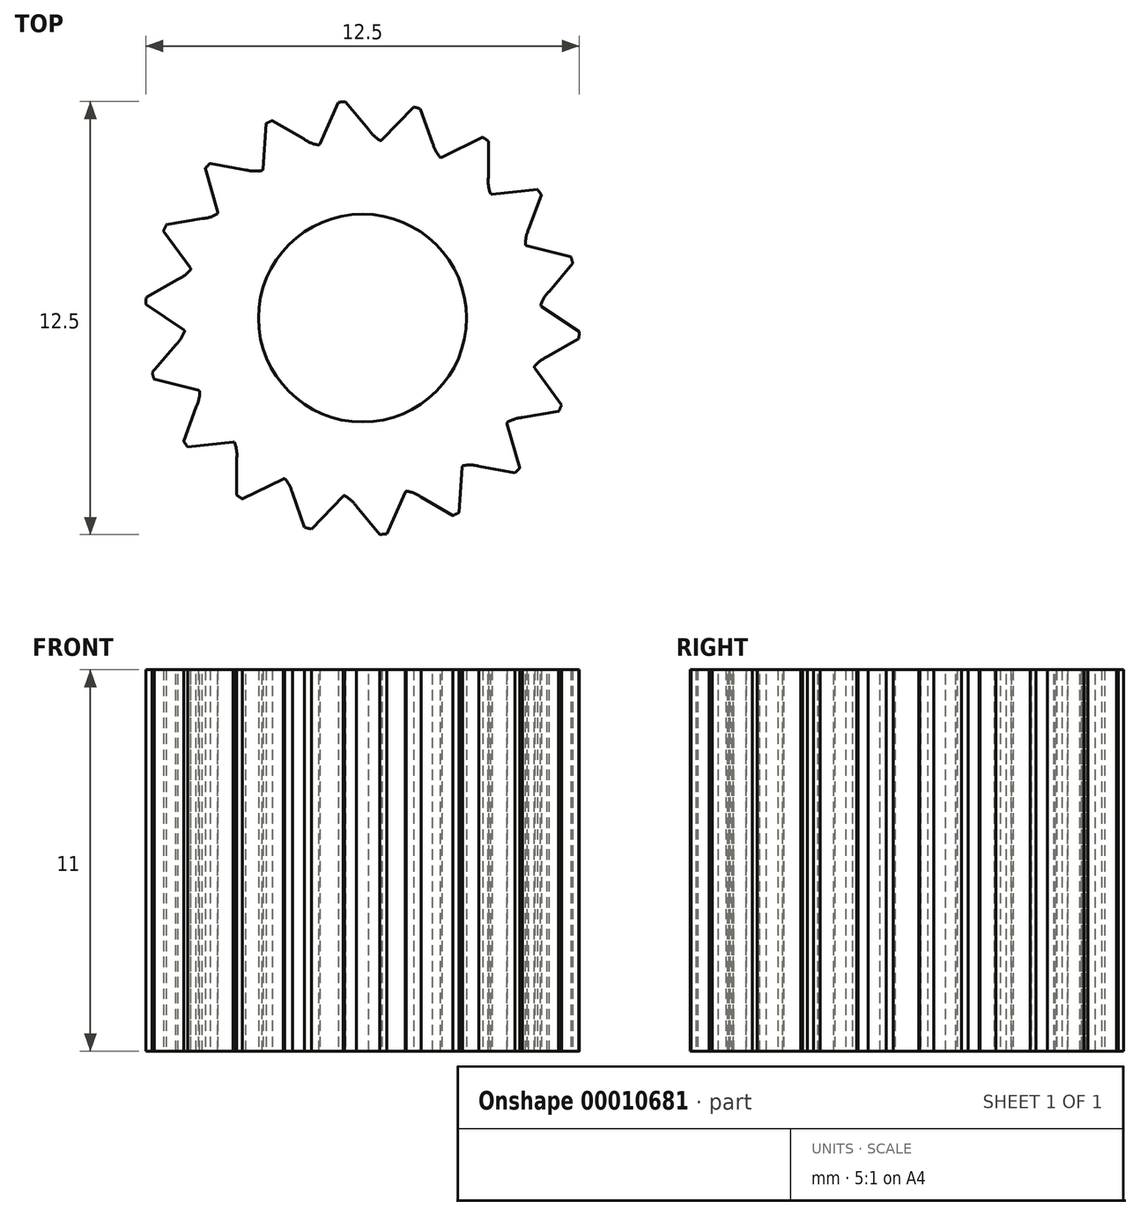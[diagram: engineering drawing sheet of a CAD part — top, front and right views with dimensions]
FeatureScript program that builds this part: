
annotation { "Feature Type Name" : "Feature", "Feature Type Description" : "" }
export const myFeature = defineFeature(function(context is Context, id is Id, definition is map)
    precondition{}
    {
        {
            var Q0;
            Q0=qCreatedBy(makeId("Top.planeOp"),FACE);
            var sketch = newSketch(context, id + "F0", { "sketchPlane" : qUnion([Q0])});
            skCircle(sketch, "E0", {"center": v(0, 0) * mm, "radius": 3 * mm});
            skCircle(sketch, "E1", {"center": v(0, 0) * mm, "radius": 6.26 * mm});
            skSolve(sketch);
        }
        {
            var Q0;
            Q0 = qSketchRegion(id + "F0", true);
            extrude(context, id + "F1", {"entities" : qUnion([Q0]), "depth" : 11 * mm});
        }
        {
            var Q0;
            Q0=qCreatedBy(makeId("Front.planeOp"),FACE);
            cPlane(context, id + "F2", {"entities" : qUnion([Q0]), "cplaneType" : CPlaneType.OFFSET, "offset" : 5 * mm, "width" : 150 * mm, "height" : 150 * mm});
        }
        {
            var Q0;
            Q0=qCreatedBy(id+"F2.planeOp",FACE);
            var sketch = newSketch(context, id + "F3", { "sketchPlane" : qUnion([Q0])});
            skLineSegment(sketch, "E2.bottom", {"start": v(0, 11.05) * mm, "end": v(-1.05, 11.05) * mm});
            skLineSegment(sketch, "E2.top", {"start": v(0, 0) * mm, "end": v(-1.05, 0) * mm});
            skLineSegment(sketch, "E2.left", {"start": v(0, 11.05) * mm, "end": v(0, 0) * mm});
            skLineSegment(sketch, "E2.right", {"start": v(-1.05, 11.05) * mm, "end": v(-1.05, 0) * mm});
            skSolve(sketch);
        }
        {
            var Q0;
            Q0=makeQuery(id+"F3.imprint","IMPRINT",FACE,{"disambiguationData":[TD([[makeQuery(id+"F3.imprint","IMPRINT",EDGE,{"derivedFrom":sQuery(id+"F3.wireOp",EDGE,"E2.bottom")}),1.0]])]});
            extrude(context, id + "F4", {"entities" : qUnion([Q0]), "depth" : 2 * mm});
        }
        {
            var Q0;
            Q0=makeQuery(id+"F4.opExtrude","CAP_EDGE",EDGE,{"disambiguationData":[OSD([sQuery(id+"F3.wireOp",EDGE,"E2.left")])],"isStart":true});
            var Q1;
            Q1=makeQuery(id+"F4.opExtrude","CAP_EDGE",EDGE,{"disambiguationData":[OSD([sQuery(id+"F3.wireOp",EDGE,"E2.right")])],"isStart":true});
            fillet(context, id + "F5", {"entities" : qUnion([Q0, Q1]), "radius" : 1 * mm, "tangentPropagation" : true, "allowEdgeOverflow" : false});
        }
        {
            var Q0;
            Q0=makeQuery(id+"F4.opExtrude","SWEPT_BODY",BODY,{"disambiguationData":[OSD([sQuery(id+"F3.wireOp",EDGE,"E2.bottom"),sQuery(id+"F3.wireOp",EDGE,"E2.top"),sQuery(id+"F3.wireOp",EDGE,"E2.left"),sQuery(id+"F3.wireOp",EDGE,"E2.right")])]});
            var Q1;
            Q1=makeQuery(id+"F1.opExtrude","SWEPT_FACE",FACE,{"disambiguationData":[OSD([sQuery(id+"F0.wireOp",EDGE,"E1")])]});
            circularPattern(context, id + "F6", {"operationType" : NewBodyOperationType.REMOVE, "entities" : qUnion([Q0]), "axis" : qUnion([Q1]), "angle" : 20 * degree, "instanceCount" : 20});
        }
        {
            var Q0;
            Q0=makeQuery(id+"F6.boolean.opBoolean","INTERSECT",EDGE,{"derivedFrom":[makeQuery(id+"F1.opExtrude","SWEPT_FACE",FACE,{"disambiguationData":[OSD([sQuery(id+"F0.wireOp",EDGE,"E1")])]}),makeQuery(id+"F6.opPattern","COPY",FACE,{"derivedFrom":makeQuery(id+"F4.opExtrude","SWEPT_FACE",FACE,{"disambiguationData":[OSD([sQuery(id+"F3.wireOp",EDGE,"E2.left")])]}),"instanceName":"1"})]});
            var Q1;
            Q1=makeQuery(id+"F6.boolean.opBoolean","INTERSECT",EDGE,{"derivedFrom":[makeQuery(id+"F1.opExtrude","SWEPT_FACE",FACE,{"disambiguationData":[OSD([sQuery(id+"F0.wireOp",EDGE,"E1")])]}),makeQuery(id+"F4.opExtrude","SWEPT_FACE",FACE,{"disambiguationData":[OSD([sQuery(id+"F3.wireOp",EDGE,"E2.left")])]})]});
            var Q2;
            Q2=makeQuery(id+"F6.boolean.opBoolean","INTERSECT",EDGE,{"derivedFrom":[makeQuery(id+"F1.opExtrude","SWEPT_FACE",FACE,{"disambiguationData":[OSD([sQuery(id+"F0.wireOp",EDGE,"E1")])]}),makeQuery(id+"F6.opPattern","COPY",FACE,{"derivedFrom":makeQuery(id+"F4.opExtrude","SWEPT_FACE",FACE,{"disambiguationData":[OSD([sQuery(id+"F3.wireOp",EDGE,"E2.left")])]}),"instanceName":"17"})]});
            var Q3;
            Q3=makeQuery(id+"F6.boolean.opBoolean","INTERSECT",EDGE,{"derivedFrom":[makeQuery(id+"F1.opExtrude","SWEPT_FACE",FACE,{"disambiguationData":[OSD([sQuery(id+"F0.wireOp",EDGE,"E1")])]}),makeQuery(id+"F6.opPattern","COPY",FACE,{"derivedFrom":makeQuery(id+"F4.opExtrude","SWEPT_FACE",FACE,{"disambiguationData":[OSD([sQuery(id+"F3.wireOp",EDGE,"E2.left")])]}),"instanceName":"16"})]});
            var Q4;
            Q4=makeQuery(id+"F6.boolean.opBoolean","INTERSECT",EDGE,{"derivedFrom":[makeQuery(id+"F1.opExtrude","SWEPT_FACE",FACE,{"disambiguationData":[OSD([sQuery(id+"F0.wireOp",EDGE,"E1")])]}),makeQuery(id+"F6.opPattern","COPY",FACE,{"derivedFrom":makeQuery(id+"F4.opExtrude","SWEPT_FACE",FACE,{"disambiguationData":[OSD([sQuery(id+"F3.wireOp",EDGE,"E2.left")])]}),"instanceName":"2"})]});
            var Q5;
            Q5=makeQuery(id+"F6.boolean.opBoolean","INTERSECT",EDGE,{"derivedFrom":[makeQuery(id+"F1.opExtrude","SWEPT_FACE",FACE,{"disambiguationData":[OSD([sQuery(id+"F0.wireOp",EDGE,"E1")])]}),makeQuery(id+"F6.opPattern","COPY",FACE,{"derivedFrom":makeQuery(id+"F4.opExtrude","SWEPT_FACE",FACE,{"disambiguationData":[OSD([sQuery(id+"F3.wireOp",EDGE,"E2.left")])]}),"instanceName":"15"})]});
            var Q6;
            Q6=makeQuery(id+"F6.boolean.opBoolean","INTERSECT",EDGE,{"derivedFrom":[makeQuery(id+"F1.opExtrude","SWEPT_FACE",FACE,{"disambiguationData":[OSD([sQuery(id+"F0.wireOp",EDGE,"E1")])]}),makeQuery(id+"F6.opPattern","COPY",FACE,{"derivedFrom":makeQuery(id+"F4.opExtrude","SWEPT_FACE",FACE,{"disambiguationData":[OSD([sQuery(id+"F3.wireOp",EDGE,"E2.left")])]}),"instanceName":"14"})]});
            var Q7;
            Q7=makeQuery(id+"F6.boolean.opBoolean","INTERSECT",EDGE,{"derivedFrom":[makeQuery(id+"F1.opExtrude","SWEPT_FACE",FACE,{"disambiguationData":[OSD([sQuery(id+"F0.wireOp",EDGE,"E1")])]}),makeQuery(id+"F6.opPattern","COPY",FACE,{"derivedFrom":makeQuery(id+"F4.opExtrude","SWEPT_FACE",FACE,{"disambiguationData":[OSD([sQuery(id+"F3.wireOp",EDGE,"E2.left")])]}),"instanceName":"3"})]});
            var Q8;
            Q8=makeQuery(id+"F6.boolean.opBoolean","INTERSECT",EDGE,{"derivedFrom":[makeQuery(id+"F1.opExtrude","SWEPT_FACE",FACE,{"disambiguationData":[OSD([sQuery(id+"F0.wireOp",EDGE,"E1")])]}),makeQuery(id+"F6.opPattern","COPY",FACE,{"derivedFrom":makeQuery(id+"F4.opExtrude","SWEPT_FACE",FACE,{"disambiguationData":[OSD([sQuery(id+"F3.wireOp",EDGE,"E2.left")])]}),"instanceName":"4"})]});
            var Q9;
            Q9=makeQuery(id+"F6.boolean.opBoolean","INTERSECT",EDGE,{"derivedFrom":[makeQuery(id+"F1.opExtrude","SWEPT_FACE",FACE,{"disambiguationData":[OSD([sQuery(id+"F0.wireOp",EDGE,"E1")])]}),makeQuery(id+"F6.opPattern","COPY",FACE,{"derivedFrom":makeQuery(id+"F4.opExtrude","SWEPT_FACE",FACE,{"disambiguationData":[OSD([sQuery(id+"F3.wireOp",EDGE,"E2.left")])]}),"instanceName":"13"})]});
            var Q10;
            Q10=makeQuery(id+"F6.boolean.opBoolean","INTERSECT",EDGE,{"derivedFrom":[makeQuery(id+"F1.opExtrude","SWEPT_FACE",FACE,{"disambiguationData":[OSD([sQuery(id+"F0.wireOp",EDGE,"E1")])]}),makeQuery(id+"F6.opPattern","COPY",FACE,{"derivedFrom":makeQuery(id+"F4.opExtrude","SWEPT_FACE",FACE,{"disambiguationData":[OSD([sQuery(id+"F3.wireOp",EDGE,"E2.left")])]}),"instanceName":"12"})]});
            var Q11;
            Q11=makeQuery(id+"F6.boolean.opBoolean","INTERSECT",EDGE,{"derivedFrom":[makeQuery(id+"F1.opExtrude","SWEPT_FACE",FACE,{"disambiguationData":[OSD([sQuery(id+"F0.wireOp",EDGE,"E1")])]}),makeQuery(id+"F6.opPattern","COPY",FACE,{"derivedFrom":makeQuery(id+"F4.opExtrude","SWEPT_FACE",FACE,{"disambiguationData":[OSD([sQuery(id+"F3.wireOp",EDGE,"E2.left")])]}),"instanceName":"11"})]});
            var Q12;
            Q12=makeQuery(id+"F6.boolean.opBoolean","INTERSECT",EDGE,{"derivedFrom":[makeQuery(id+"F1.opExtrude","SWEPT_FACE",FACE,{"disambiguationData":[OSD([sQuery(id+"F0.wireOp",EDGE,"E1")])]}),makeQuery(id+"F6.opPattern","COPY",FACE,{"derivedFrom":makeQuery(id+"F4.opExtrude","SWEPT_FACE",FACE,{"disambiguationData":[OSD([sQuery(id+"F3.wireOp",EDGE,"E2.left")])]}),"instanceName":"10"})]});
            var Q13;
            Q13=makeQuery(id+"F6.boolean.opBoolean","INTERSECT",EDGE,{"derivedFrom":[makeQuery(id+"F1.opExtrude","SWEPT_FACE",FACE,{"disambiguationData":[OSD([sQuery(id+"F0.wireOp",EDGE,"E1")])]}),makeQuery(id+"F6.opPattern","COPY",FACE,{"derivedFrom":makeQuery(id+"F4.opExtrude","SWEPT_FACE",FACE,{"disambiguationData":[OSD([sQuery(id+"F3.wireOp",EDGE,"E2.left")])]}),"instanceName":"9"})]});
            var Q14;
            Q14=makeQuery(id+"F6.boolean.opBoolean","INTERSECT",EDGE,{"derivedFrom":[makeQuery(id+"F1.opExtrude","SWEPT_FACE",FACE,{"disambiguationData":[OSD([sQuery(id+"F0.wireOp",EDGE,"E1")])]}),makeQuery(id+"F6.opPattern","COPY",FACE,{"derivedFrom":makeQuery(id+"F4.opExtrude","SWEPT_FACE",FACE,{"disambiguationData":[OSD([sQuery(id+"F3.wireOp",EDGE,"E2.left")])]}),"instanceName":"8"})]});
            var Q15;
            Q15=makeQuery(id+"F6.boolean.opBoolean","INTERSECT",EDGE,{"derivedFrom":[makeQuery(id+"F1.opExtrude","SWEPT_FACE",FACE,{"disambiguationData":[OSD([sQuery(id+"F0.wireOp",EDGE,"E1")])]}),makeQuery(id+"F6.opPattern","COPY",FACE,{"derivedFrom":makeQuery(id+"F4.opExtrude","SWEPT_FACE",FACE,{"disambiguationData":[OSD([sQuery(id+"F3.wireOp",EDGE,"E2.left")])]}),"instanceName":"7"})]});
            var Q16;
            Q16=makeQuery(id+"F6.boolean.opBoolean","INTERSECT",EDGE,{"derivedFrom":[makeQuery(id+"F1.opExtrude","SWEPT_FACE",FACE,{"disambiguationData":[OSD([sQuery(id+"F0.wireOp",EDGE,"E1")])]}),makeQuery(id+"F6.opPattern","COPY",FACE,{"derivedFrom":makeQuery(id+"F4.opExtrude","SWEPT_FACE",FACE,{"disambiguationData":[OSD([sQuery(id+"F3.wireOp",EDGE,"E2.left")])]}),"instanceName":"6"})]});
            var Q17;
            Q17=makeQuery(id+"F6.boolean.opBoolean","INTERSECT",EDGE,{"derivedFrom":[makeQuery(id+"F1.opExtrude","SWEPT_FACE",FACE,{"disambiguationData":[OSD([sQuery(id+"F0.wireOp",EDGE,"E1")])]}),makeQuery(id+"F6.opPattern","COPY",FACE,{"derivedFrom":makeQuery(id+"F4.opExtrude","SWEPT_FACE",FACE,{"disambiguationData":[OSD([sQuery(id+"F3.wireOp",EDGE,"E2.left")])]}),"instanceName":"5"})]});
            chamfer(context, id + "F7", {"entities" : qUnion([Q0, Q1, Q2, Q3, Q4, Q5, Q6, Q7, Q8, Q9, Q10, Q11, Q12, Q13, Q14, Q15, Q16, Q17]), "chamferType" : ChamferType.OFFSET_ANGLE, "width" : 0.7 * mm, "oppositeDirection" : false, "angle" : 60 * degree, "tangentPropagation" : true});
        }
        {
            var Q0;
            Q0=makeQuery(id+"F6.boolean.opBoolean","INTERSECT",EDGE,{"derivedFrom":[makeQuery(id+"F1.opExtrude","SWEPT_FACE",FACE,{"disambiguationData":[OSD([sQuery(id+"F0.wireOp",EDGE,"E1")])]}),makeQuery(id+"F6.opPattern","COPY",FACE,{"derivedFrom":makeQuery(id+"F4.opExtrude","SWEPT_FACE",FACE,{"disambiguationData":[OSD([sQuery(id+"F3.wireOp",EDGE,"E2.right")])]}),"instanceName":"3"})]});
            var Q1;
            Q1=makeQuery(id+"F6.boolean.opBoolean","INTERSECT",EDGE,{"derivedFrom":[makeQuery(id+"F1.opExtrude","SWEPT_FACE",FACE,{"disambiguationData":[OSD([sQuery(id+"F0.wireOp",EDGE,"E1")])]}),makeQuery(id+"F6.opPattern","COPY",FACE,{"derivedFrom":makeQuery(id+"F4.opExtrude","SWEPT_FACE",FACE,{"disambiguationData":[OSD([sQuery(id+"F3.wireOp",EDGE,"E2.right")])]}),"instanceName":"4"})]});
            var Q2;
            Q2=makeQuery(id+"F6.boolean.opBoolean","INTERSECT",EDGE,{"derivedFrom":[makeQuery(id+"F1.opExtrude","SWEPT_FACE",FACE,{"disambiguationData":[OSD([sQuery(id+"F0.wireOp",EDGE,"E1")])]}),makeQuery(id+"F6.opPattern","COPY",FACE,{"derivedFrom":makeQuery(id+"F4.opExtrude","SWEPT_FACE",FACE,{"disambiguationData":[OSD([sQuery(id+"F3.wireOp",EDGE,"E2.right")])]}),"instanceName":"5"})]});
            var Q3;
            Q3=makeQuery(id+"F6.boolean.opBoolean","INTERSECT",EDGE,{"derivedFrom":[makeQuery(id+"F1.opExtrude","SWEPT_FACE",FACE,{"disambiguationData":[OSD([sQuery(id+"F0.wireOp",EDGE,"E1")])]}),makeQuery(id+"F6.opPattern","COPY",FACE,{"derivedFrom":makeQuery(id+"F4.opExtrude","SWEPT_FACE",FACE,{"disambiguationData":[OSD([sQuery(id+"F3.wireOp",EDGE,"E2.right")])]}),"instanceName":"6"})]});
            var Q4;
            Q4=makeQuery(id+"F6.boolean.opBoolean","INTERSECT",EDGE,{"derivedFrom":[makeQuery(id+"F1.opExtrude","SWEPT_FACE",FACE,{"disambiguationData":[OSD([sQuery(id+"F0.wireOp",EDGE,"E1")])]}),makeQuery(id+"F6.opPattern","COPY",FACE,{"derivedFrom":makeQuery(id+"F4.opExtrude","SWEPT_FACE",FACE,{"disambiguationData":[OSD([sQuery(id+"F3.wireOp",EDGE,"E2.right")])]}),"instanceName":"2"})]});
            var Q5;
            Q5=makeQuery(id+"F6.boolean.opBoolean","INTERSECT",EDGE,{"derivedFrom":[makeQuery(id+"F1.opExtrude","SWEPT_FACE",FACE,{"disambiguationData":[OSD([sQuery(id+"F0.wireOp",EDGE,"E1")])]}),makeQuery(id+"F6.opPattern","COPY",FACE,{"derivedFrom":makeQuery(id+"F4.opExtrude","SWEPT_FACE",FACE,{"disambiguationData":[OSD([sQuery(id+"F3.wireOp",EDGE,"E2.right")])]}),"instanceName":"1"})]});
            var Q6;
            Q6=makeQuery(id+"F6.boolean.opBoolean","INTERSECT",EDGE,{"derivedFrom":[makeQuery(id+"F1.opExtrude","SWEPT_FACE",FACE,{"disambiguationData":[OSD([sQuery(id+"F0.wireOp",EDGE,"E1")])]}),makeQuery(id+"F4.opExtrude","SWEPT_FACE",FACE,{"disambiguationData":[OSD([sQuery(id+"F3.wireOp",EDGE,"E2.right")])]})]});
            var Q7;
            Q7=makeQuery(id+"F6.boolean.opBoolean","INTERSECT",EDGE,{"derivedFrom":[makeQuery(id+"F1.opExtrude","SWEPT_FACE",FACE,{"disambiguationData":[OSD([sQuery(id+"F0.wireOp",EDGE,"E1")])]}),makeQuery(id+"F6.opPattern","COPY",FACE,{"derivedFrom":makeQuery(id+"F4.opExtrude","SWEPT_FACE",FACE,{"disambiguationData":[OSD([sQuery(id+"F3.wireOp",EDGE,"E2.right")])]}),"instanceName":"17"})]});
            var Q8;
            Q8=makeQuery(id+"F6.boolean.opBoolean","INTERSECT",EDGE,{"derivedFrom":[makeQuery(id+"F1.opExtrude","SWEPT_FACE",FACE,{"disambiguationData":[OSD([sQuery(id+"F0.wireOp",EDGE,"E1")])]}),makeQuery(id+"F6.opPattern","COPY",FACE,{"derivedFrom":makeQuery(id+"F4.opExtrude","SWEPT_FACE",FACE,{"disambiguationData":[OSD([sQuery(id+"F3.wireOp",EDGE,"E2.right")])]}),"instanceName":"16"})]});
            var Q9;
            Q9=makeQuery(id+"F6.boolean.opBoolean","INTERSECT",EDGE,{"derivedFrom":[makeQuery(id+"F1.opExtrude","SWEPT_FACE",FACE,{"disambiguationData":[OSD([sQuery(id+"F0.wireOp",EDGE,"E1")])]}),makeQuery(id+"F6.opPattern","COPY",FACE,{"derivedFrom":makeQuery(id+"F4.opExtrude","SWEPT_FACE",FACE,{"disambiguationData":[OSD([sQuery(id+"F3.wireOp",EDGE,"E2.right")])]}),"instanceName":"15"})]});
            var Q10;
            Q10=makeQuery(id+"F6.boolean.opBoolean","INTERSECT",EDGE,{"derivedFrom":[makeQuery(id+"F1.opExtrude","SWEPT_FACE",FACE,{"disambiguationData":[OSD([sQuery(id+"F0.wireOp",EDGE,"E1")])]}),makeQuery(id+"F6.opPattern","COPY",FACE,{"derivedFrom":makeQuery(id+"F4.opExtrude","SWEPT_FACE",FACE,{"disambiguationData":[OSD([sQuery(id+"F3.wireOp",EDGE,"E2.right")])]}),"instanceName":"14"})]});
            var Q11;
            Q11=makeQuery(id+"F6.boolean.opBoolean","INTERSECT",EDGE,{"derivedFrom":[makeQuery(id+"F1.opExtrude","SWEPT_FACE",FACE,{"disambiguationData":[OSD([sQuery(id+"F0.wireOp",EDGE,"E1")])]}),makeQuery(id+"F6.opPattern","COPY",FACE,{"derivedFrom":makeQuery(id+"F4.opExtrude","SWEPT_FACE",FACE,{"disambiguationData":[OSD([sQuery(id+"F3.wireOp",EDGE,"E2.right")])]}),"instanceName":"12"})]});
            var Q12;
            Q12=makeQuery(id+"F6.boolean.opBoolean","INTERSECT",EDGE,{"derivedFrom":[makeQuery(id+"F1.opExtrude","SWEPT_FACE",FACE,{"disambiguationData":[OSD([sQuery(id+"F0.wireOp",EDGE,"E1")])]}),makeQuery(id+"F6.opPattern","COPY",FACE,{"derivedFrom":makeQuery(id+"F4.opExtrude","SWEPT_FACE",FACE,{"disambiguationData":[OSD([sQuery(id+"F3.wireOp",EDGE,"E2.right")])]}),"instanceName":"11"})]});
            var Q13;
            Q13=makeQuery(id+"F6.boolean.opBoolean","INTERSECT",EDGE,{"derivedFrom":[makeQuery(id+"F1.opExtrude","SWEPT_FACE",FACE,{"disambiguationData":[OSD([sQuery(id+"F0.wireOp",EDGE,"E1")])]}),makeQuery(id+"F6.opPattern","COPY",FACE,{"derivedFrom":makeQuery(id+"F4.opExtrude","SWEPT_FACE",FACE,{"disambiguationData":[OSD([sQuery(id+"F3.wireOp",EDGE,"E2.right")])]}),"instanceName":"10"})]});
            var Q14;
            Q14=makeQuery(id+"F6.boolean.opBoolean","INTERSECT",EDGE,{"derivedFrom":[makeQuery(id+"F1.opExtrude","SWEPT_FACE",FACE,{"disambiguationData":[OSD([sQuery(id+"F0.wireOp",EDGE,"E1")])]}),makeQuery(id+"F6.opPattern","COPY",FACE,{"derivedFrom":makeQuery(id+"F4.opExtrude","SWEPT_FACE",FACE,{"disambiguationData":[OSD([sQuery(id+"F3.wireOp",EDGE,"E2.right")])]}),"instanceName":"9"})]});
            var Q15;
            Q15=makeQuery(id+"F6.boolean.opBoolean","INTERSECT",EDGE,{"derivedFrom":[makeQuery(id+"F1.opExtrude","SWEPT_FACE",FACE,{"disambiguationData":[OSD([sQuery(id+"F0.wireOp",EDGE,"E1")])]}),makeQuery(id+"F6.opPattern","COPY",FACE,{"derivedFrom":makeQuery(id+"F4.opExtrude","SWEPT_FACE",FACE,{"disambiguationData":[OSD([sQuery(id+"F3.wireOp",EDGE,"E2.right")])]}),"instanceName":"8"})]});
            var Q16;
            Q16=makeQuery(id+"F6.boolean.opBoolean","INTERSECT",EDGE,{"derivedFrom":[makeQuery(id+"F1.opExtrude","SWEPT_FACE",FACE,{"disambiguationData":[OSD([sQuery(id+"F0.wireOp",EDGE,"E1")])]}),makeQuery(id+"F6.opPattern","COPY",FACE,{"derivedFrom":makeQuery(id+"F4.opExtrude","SWEPT_FACE",FACE,{"disambiguationData":[OSD([sQuery(id+"F3.wireOp",EDGE,"E2.right")])]}),"instanceName":"7"})]});
            var Q17;
            Q17=makeQuery(id+"F6.boolean.opBoolean","INTERSECT",EDGE,{"derivedFrom":[makeQuery(id+"F1.opExtrude","SWEPT_FACE",FACE,{"disambiguationData":[OSD([sQuery(id+"F0.wireOp",EDGE,"E1")])]}),makeQuery(id+"F6.opPattern","COPY",FACE,{"derivedFrom":makeQuery(id+"F4.opExtrude","SWEPT_FACE",FACE,{"disambiguationData":[OSD([sQuery(id+"F3.wireOp",EDGE,"E2.right")])]}),"instanceName":"13"})]});
            chamfer(context, id + "F8", {"entities" : qUnion([Q0, Q1, Q2, Q3, Q4, Q5, Q6, Q7, Q8, Q9, Q10, Q11, Q12, Q13, Q14, Q15, Q16, Q17]), "chamferType" : ChamferType.OFFSET_ANGLE, "width" : 2 * mm, "oppositeDirection" : false, "angle" : 35 * degree, "tangentPropagation" : true});
        }
    });
